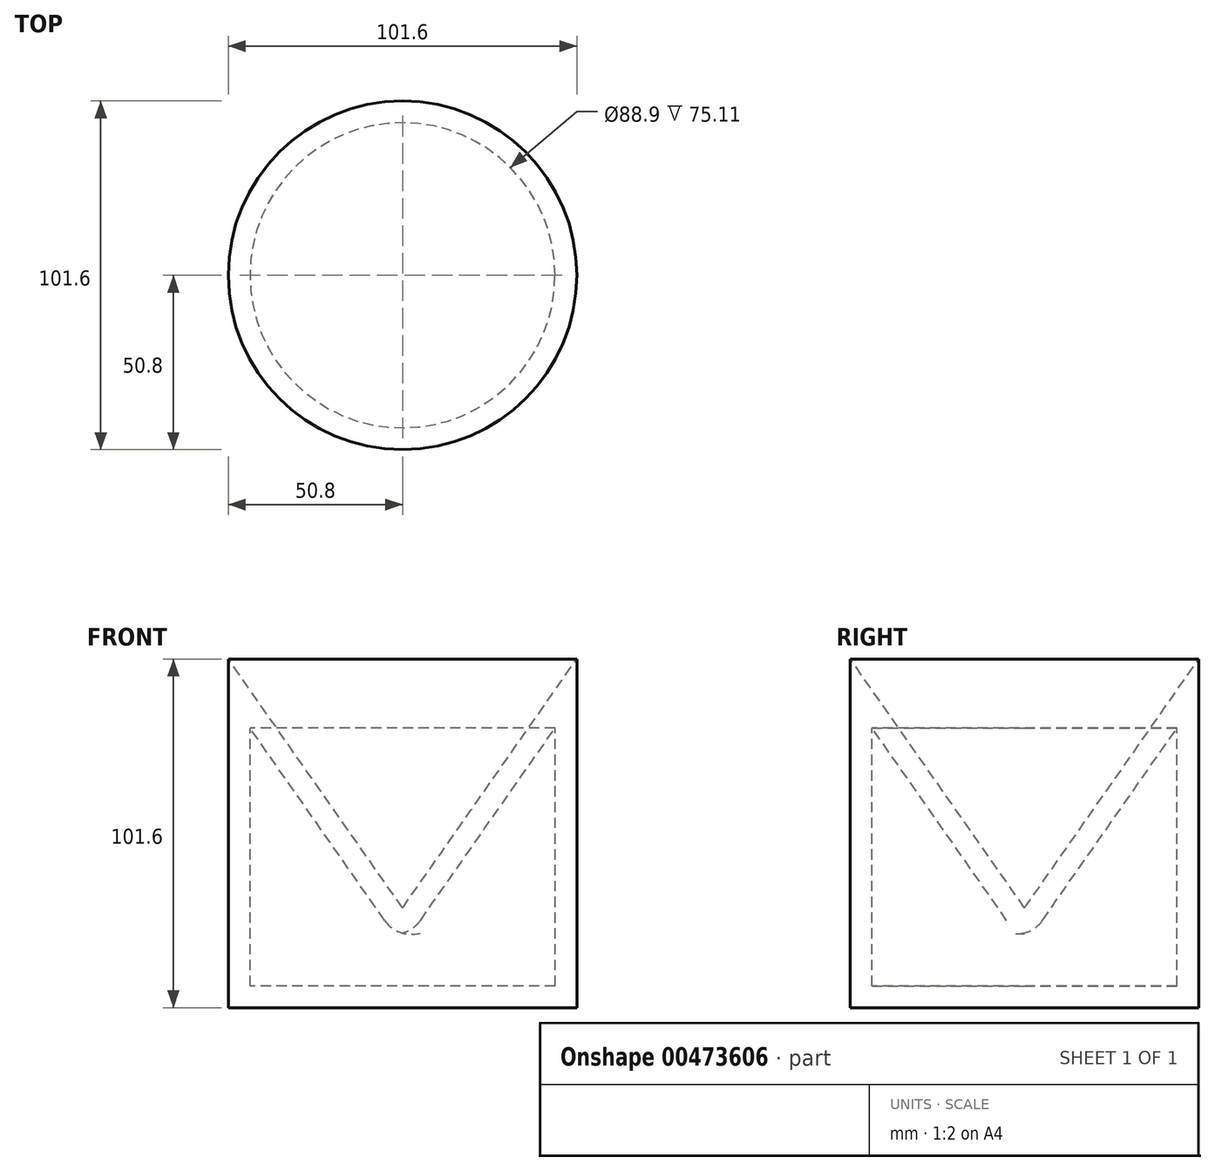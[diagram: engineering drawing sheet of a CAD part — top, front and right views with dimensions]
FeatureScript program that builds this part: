
annotation { "Feature Type Name" : "Feature", "Feature Type Description" : "" }
export const myFeature = defineFeature(function(context is Context, id is Id, definition is map)
    precondition{}
    {
        {
            var Q0;
            Q0=qCreatedBy(makeId("Front.planeOp"),FACE);
            var sketch = newSketch(context, id + "F0", { "sketchPlane" : qUnion([Q0])});
            skLineSegment(sketch, "E0", {"start": v(0, 0) * mm, "end": v(50.8, 0) * mm});
            skLineSegment(sketch, "E1", {"start": v(50.8, 0) * mm, "end": v(50.8, 101.6) * mm});
            skLineSegment(sketch, "E2", {"start": v(50.8, 101.6) * mm, "end": v(0, 29.05) * mm});
            skLineSegment(sketch, "E3", {"start": v(0, 29.05) * mm, "end": v(0, 0) * mm});
            skLineSegment(sketch, "E4.0", {"start": v(44.45, 81.46) * mm, "end": v(5.2, 25.4) * mm});
            skLineSegment(sketch, "E4.1", {"start": v(44.45, 6.35) * mm, "end": v(44.45, 81.46) * mm});
            skLineSegment(sketch, "E4.2", {"start": v(0, 6.35) * mm, "end": v(44.45, 6.35) * mm});
            skArc(sketch, "E5", {"start": v(5.2, 25.4) * mm, "mid": v(2.92, 23.11) * mm, "end": v(0, 21.72) * mm});
            skSolve(sketch);
        }
        {
            var Q0;
            {var subQ3=sQuery(id+"F0.wireOp",EDGE,"E0");Q0=makeQuery(id+"F0.imprint","IMPRINT",FACE,{"disambiguationData":[TD([[makeQuery(id+"F0.imprint","IMPRINT",EDGE,{"derivedFrom":subQ3}),1.0]])]});}
            var Q1;
            Q1=sQuery(id+"F0.wireOp",EDGE,"E3");
            revolve(context, id + "F1", {"entities" : qUnion([Q0]), "axis" : qUnion([Q1]), "revolveType" : RevolveType.FULL});
        }
    });
